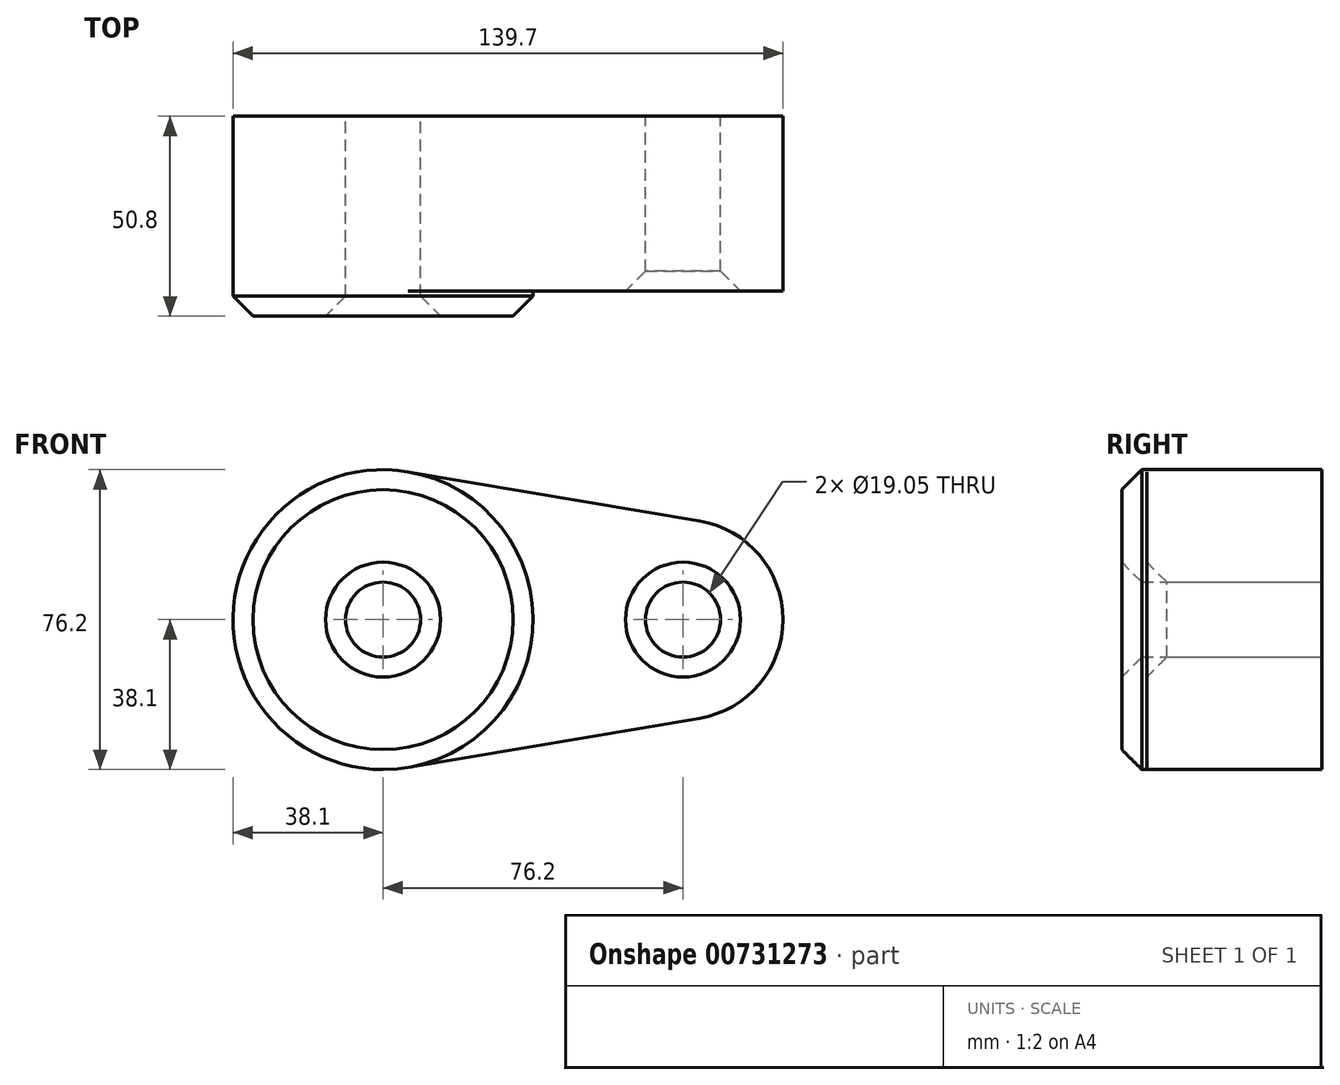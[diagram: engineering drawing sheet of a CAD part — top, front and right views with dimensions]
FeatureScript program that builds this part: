
annotation { "Feature Type Name" : "Feature", "Feature Type Description" : "" }
export const myFeature = defineFeature(function(context is Context, id is Id, definition is map)
    precondition{}
    {
        {
            var Q0;
            Q0=qCreatedBy(makeId("Front.planeOp"),FACE);
            var sketch = newSketch(context, id + "F0", { "sketchPlane" : qUnion([Q0])});
            skCircle(sketch, "E0", {"center": v(0, 0) * mm, "radius": 38.1 * mm});
            skCircle(sketch, "E1", {"center": v(76.2, 0) * mm, "radius": 25.4 * mm});
            skLineSegment(sketch, "E2", {"start": v(6.35, 37.57) * mm, "end": v(80.43, 25.04) * mm});
            skLineSegment(sketch, "E3", {"start": v(6.35, -37.57) * mm, "end": v(80.43, -25.04) * mm});
            skCircle(sketch, "E4", {"center": v(0, 0) * mm, "radius": 9.53 * mm});
            skCircle(sketch, "E5", {"center": v(76.2, 0) * mm, "radius": 9.53 * mm});
            skSolve(sketch);
        }
        {
            var Q0;
            Q0=makeQuery(id+"F0.imprint","IMPRINT",FACE,{"disambiguationData":[TD([[makeQuery(id+"F0.imprint","IMPRINT",EDGE,{"derivedFrom":sQuery(id+"F0.wireOp",EDGE,"E4")}),-1.0]])]});
            var Q1;
            Q1=sQuery(id+"F0.wireOp",EDGE,"E0");
            extrude(context, id + "F1", {"entities" : qUnion([Q0]), "surfaceEntities" : qUnion([Q1]), "depth" : 30.7 * mm, "offsetDistance" : 25.4 * mm, "hasDraft" : true, "draftAngle" : 3 * degree, "draftPullDirection" : true});
        }
        {
            var Q0;
            Q0=makeQuery(id+"F0.imprint","IMPRINT",FACE,{"disambiguationData":[TD([[makeQuery(id+"F0.imprint","IMPRINT",EDGE,{"derivedFrom":sQuery(id+"F0.wireOp",EDGE,"E4")}),-1.0]])]});
            extrude(context, id + "F2", {"entities" : qUnion([Q0]), "operationType" : NewBodyOperationType.ADD, "depth" : 50.8 * mm, "offsetDistance" : 25.4 * mm});
        }
        {
            var Q0;
            {var subQ0=sQuery(id+"F0.wireOp",EDGE,"E2");Q0=makeQuery(id+"F0.imprint","IMPRINT",FACE,{"disambiguationData":[TD([[makeQuery(id+"F0.imprint","IMPRINT",EDGE,{"derivedFrom":subQ0}),-1.0]])]});}
            var Q1;
            Q1=makeQuery(id+"F0.imprint","IMPRINT",FACE,{"disambiguationData":[TD([[makeQuery(id+"F0.imprint","IMPRINT",EDGE,{"derivedFrom":sQuery(id+"F0.wireOp",EDGE,"E5")}),-1.0]])]});
            extrude(context, id + "F3", {"entities" : qUnion([Q0, Q1]), "operationType" : NewBodyOperationType.ADD, "depth" : 44.45 * mm, "offsetDistance" : 25.4 * mm});
        }
        {
            var Q0;
            Q0=makeQuery(id+"F2.opExtrude","CAP_EDGE",EDGE,{"disambiguationData":[OSD([sQuery(id+"F0.wireOp",EDGE,"E4")])],"isStart":false});
            var Q1;
            Q1=makeQuery(id+"F2.opExtrude","CAP_EDGE",EDGE,{"disambiguationData":[OSD([sQuery(id+"F0.wireOp",EDGE,"E0")])],"isStart":false});
            var Q2;
            Q2=makeQuery(id+"F3.opExtrude","CAP_EDGE",EDGE,{"disambiguationData":[OSD([sQuery(id+"F0.wireOp",EDGE,"E5")])],"isStart":false});
            chamfer(context, id + "F4", {"entities" : qUnion([Q0, Q1, Q2]), "width" : 5.08 * mm, "tangentPropagation" : true});
        }
    });
